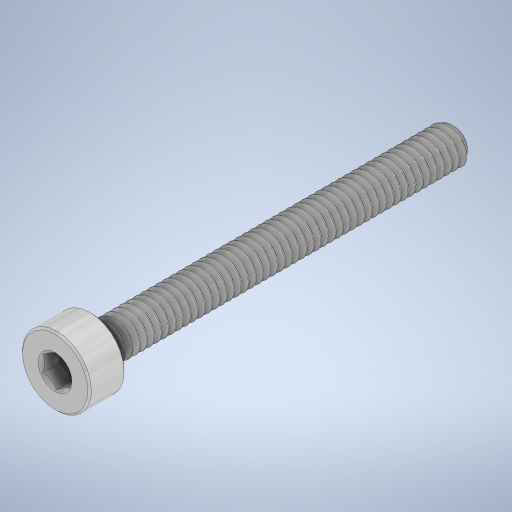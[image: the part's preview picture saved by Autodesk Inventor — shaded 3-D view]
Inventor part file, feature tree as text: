
AUTODESK INVENTOR PART (.ipt)
format: ipt  version: 2023 (Build 270158000, 158)  size: 1,028,096 bytes
history: native  units: in
note: dims shown in document units (in); Inventor stores cm internally (conversion verified against a paired STEP export)
features: revolve x1
ambient origin geometry x8: Origin, YZ Plane, XZ Plane, XY Plane, X Axis, Y Axis, Z Axis, Center Point
bodies: Solid1 (feature_tree)
feature tree (1):
  revolve  "Revolve2"  [1 undecoded]
note: 1 required parameter value undecoded (feature->parameter linkage not recoverable at this tier; creation-order binding heuristic only, values carry confidence <= 0.55)
